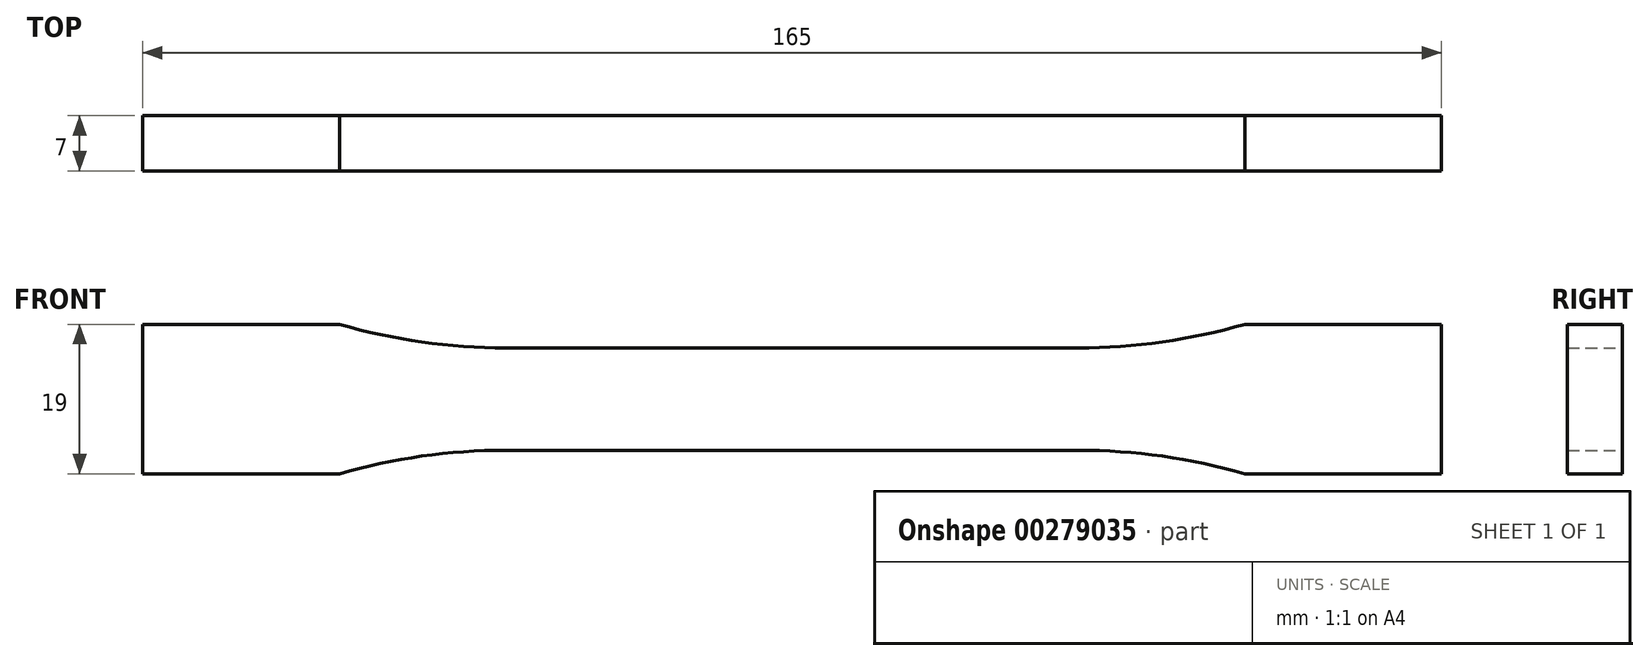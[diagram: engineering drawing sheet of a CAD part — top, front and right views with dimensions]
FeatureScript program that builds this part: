
annotation { "Feature Type Name" : "Feature", "Feature Type Description" : "" }
export const myFeature = defineFeature(function(context is Context, id is Id, definition is map)
    precondition{}
    {
        {
            var Q0;
            Q0=qCreatedBy(makeId("Front.planeOp"),FACE);
            var sketch = newSketch(context, id + "F0", { "sketchPlane" : qUnion([Q0])});
            skLineSegment(sketch, "E0", {"start": v(0, 6.5) * mm, "end": v(36.36, 6.5) * mm});
            skArc(sketch, "E1", {"start": v(36.36, 6.5) * mm, "mid": v(47.03, 7.25) * mm, "end": v(57.5, 9.5) * mm});
            skLineSegment(sketch, "E2", {"start": v(57.5, 9.5) * mm, "end": v(82.5, 9.5) * mm});
            skLineSegment(sketch, "E3.MirrorCS", {"start": v(57.5, -9.5) * mm, "end": v(82.5, -9.5) * mm});
            skLineSegment(sketch, "E4.MirrorCS", {"start": v(0, -6.5) * mm, "end": v(36.36, -6.5) * mm});
            skArc(sketch, "E5.MirrorCS", {"start": v(36.36, -6.5) * mm, "mid": v(47.03, -7.25) * mm, "end": v(57.5, -9.5) * mm});
            skArc(sketch, "E6.MirrorCS", {"start": v(-36.36, -6.5) * mm, "mid": v(-47.03, -7.25) * mm, "end": v(-57.5, -9.5) * mm});
            skLineSegment(sketch, "E7.MirrorCS", {"start": v(0, 6.5) * mm, "end": v(-36.36, 6.5) * mm});
            skArc(sketch, "E8.MirrorCS", {"start": v(-36.36, 6.5) * mm, "mid": v(-47.03, 7.25) * mm, "end": v(-57.5, 9.5) * mm});
            skLineSegment(sketch, "E9.MirrorCS", {"start": v(-57.5, -9.5) * mm, "end": v(-82.5, -9.5) * mm});
            skLineSegment(sketch, "E10.MirrorCS", {"start": v(0, -6.5) * mm, "end": v(-36.36, -6.5) * mm});
            skLineSegment(sketch, "E11.MirrorCS", {"start": v(-57.5, 9.5) * mm, "end": v(-82.5, 9.5) * mm});
            skLineSegment(sketch, "E12", {"start": v(-82.5, 9.5) * mm, "end": v(-82.5, -9.5) * mm});
            skLineSegment(sketch, "E13", {"start": v(82.5, 9.5) * mm, "end": v(82.5, -9.5) * mm});
            skSolve(sketch);
        }
        {
            var Q0;
            Q0 = qSketchRegion(id + "F0", true);
            extrude(context, id + "F1", {"entities" : qUnion([Q0]), "endBound" : BoundingType.SYMMETRIC, "depth" : 7 * mm});
        }
    });
